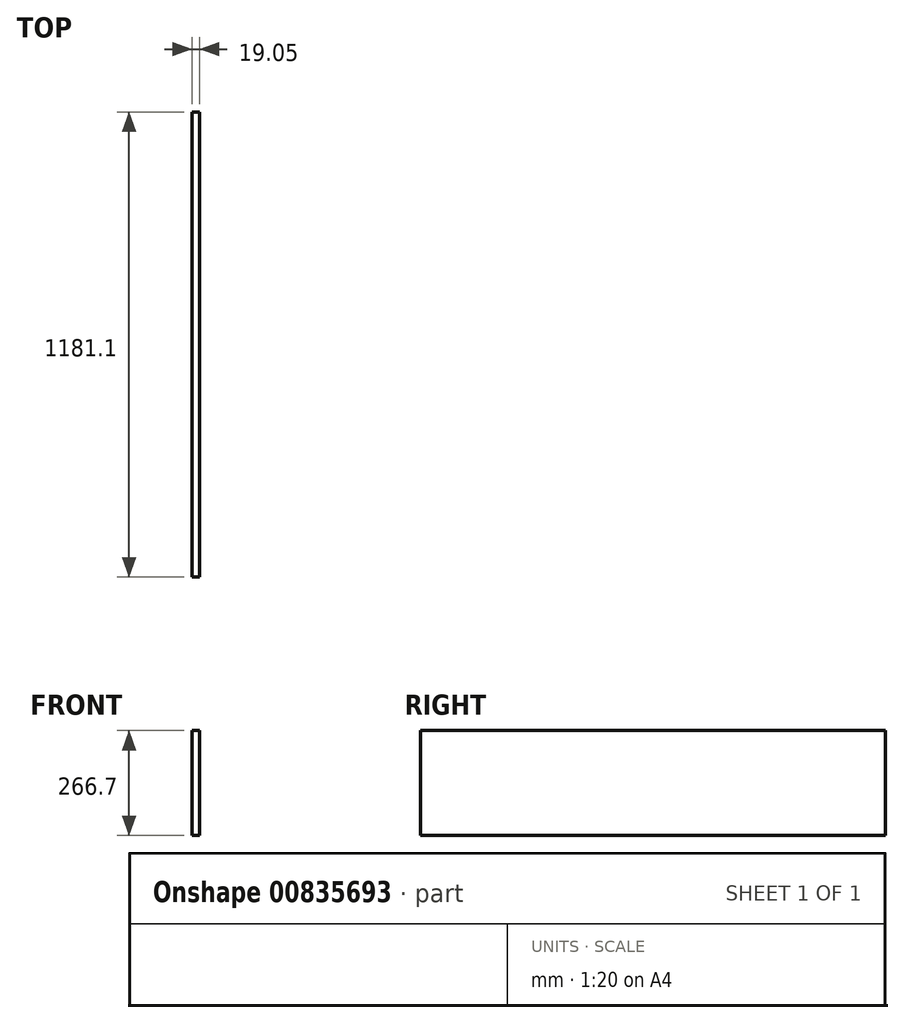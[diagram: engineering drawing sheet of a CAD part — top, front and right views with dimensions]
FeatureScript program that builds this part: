
annotation { "Feature Type Name" : "Feature", "Feature Type Description" : "" }
export const myFeature = defineFeature(function(context is Context, id is Id, definition is map)
    precondition{}
    {
        {
            var Q0;
            Q0=qCreatedBy(makeId("Right.planeOp"),FACE);
            var sketch = newSketch(context, id + "F0", { "sketchPlane" : qUnion([Q0])});
            skLineSegment(sketch, "E0.bottom", {"start": v(0, 0) * mm, "end": v(1181.1, 0) * mm});
            skLineSegment(sketch, "E0.top", {"start": v(0, 266.7) * mm, "end": v(1181.1, 266.7) * mm});
            skLineSegment(sketch, "E0.left", {"start": v(0, 0) * mm, "end": v(0, 266.7) * mm});
            skLineSegment(sketch, "E0.right", {"start": v(1181.1, 0) * mm, "end": v(1181.1, 266.7) * mm});
            skSolve(sketch);
        }
        {
            var Q0;
            Q0=qSketchRegion(id+"F0",true);
            extrude(context, id + "F1", {"entities" : qUnion([Q0]), "depth" : 19.05 * mm, "offsetDistance" : 25.4 * mm});
        }
    });
